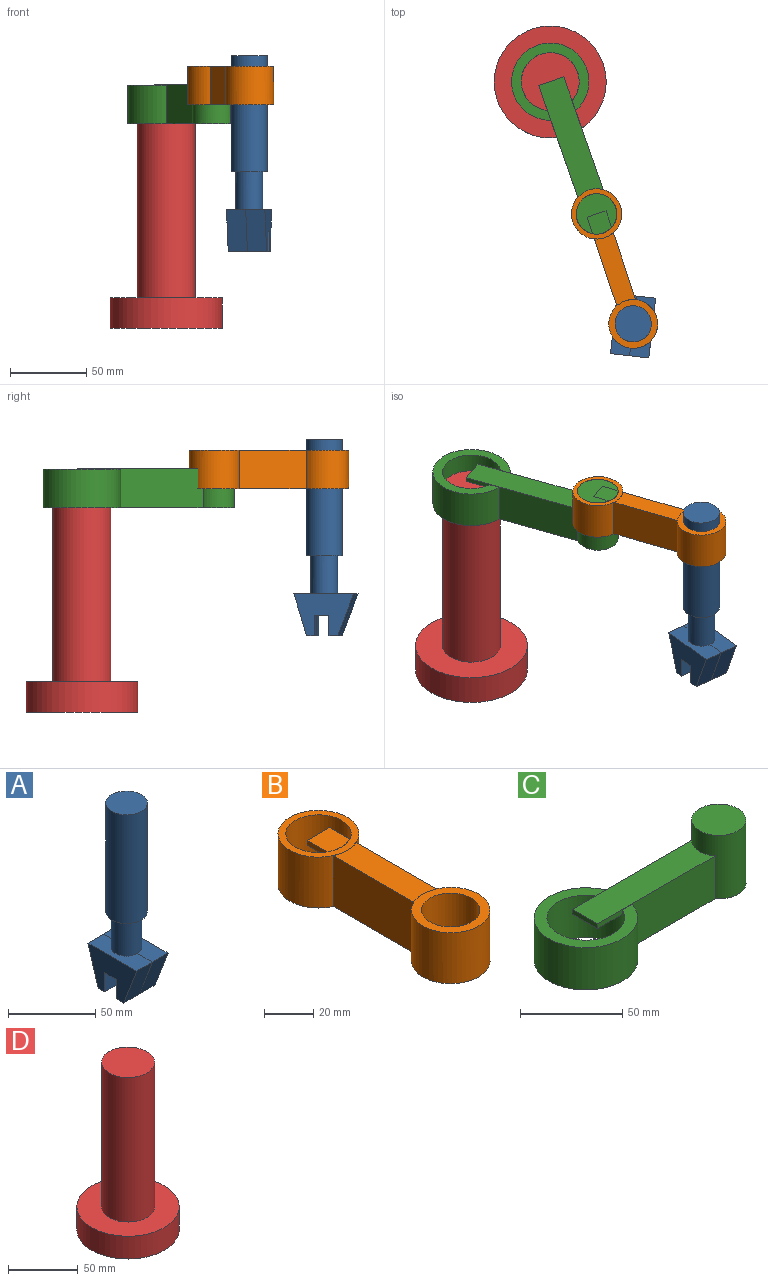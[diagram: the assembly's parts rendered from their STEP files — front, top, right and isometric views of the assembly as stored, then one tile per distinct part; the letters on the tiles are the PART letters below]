
ASSEMBLY  parts=4 mates=3
PART A: 23 faces, bbox 25.4x39.5x128.8 mm
  f0: cylinder r=8.8mm len=25.07mm, axis (0,0,1), area 1386.8mm2, adj f3,f4,f13,f14,f16
  f1: cylinder r=11.91mm len=76.2mm, axis (0,0,-1), area 5703.5mm2, adj f2,f3
  f2: plane 23.83x23.83mm, normal (0,0,1), area 445.8mm2, adj f1
  f3: plane 23.83x23.83mm, normal (0,0,-1), area 202.3mm2, adj f0,f1
  f4: plane 39.49x12.7mm, normal (0,0,1), area 379.8mm2, adj f0,f5,f11,f12,f13,f14
  f5: plane 27.55x12.71mm, normal (0,-0.93,-0.36), area 374.1mm2, adj f4,f6,f12,f17
  f6: plane 25.4x5.91mm, normal (0,0,-1), area 150.1mm2, adj f5,f7,f12,f17,f18,f22
  f7: plane 13.52x12.71mm, normal (0,1,0), area 171.6mm2, adj f6,f8,f12,f18
  f8: plane 12.71x9.62mm, normal (0,0,-1), area 122.1mm2, adj f7,f9,f12,f19
  f9: plane 13.51x12.7mm, normal (0,-1,0), area 171.6mm2, adj f8,f10,f12,f20
  f10: plane 12.71x5.2mm, normal (0,0,-1), area 66mm2, adj f9,f11,f12,f21
  f11: plane 27.54x12.7mm, normal (0,0.96,-0.29), area 365.4mm2, adj f4,f10,f12,f15
  f12: plane 39.49x27.54mm, normal (1,0,0), area 699.2mm2, adj f4,f5,f6,f7,f8,f9,f10,f11
  f13: plane 12.11x0.01mm, normal (1,0,0), area 0.1mm2, adj f0,f4,f16
  f14: plane 9.77x0mm, normal (1,0,0), area 0mm2, adj f0,f4,f16
  f15: plane 27.55x12.7mm, normal (0,0.96,-0.29), area 365.4mm2, adj f11,f16,f21,f22
  f16: plane 39.49x12.7mm, normal (0,0,1), area 379.8mm2, adj f0,f13,f14,f15,f17,f22
  f17: plane 27.56x12.71mm, normal (0,-0.93,-0.36), area 374.3mm2, adj f5,f6,f16,f22
  f18: plane 13.52x12.71mm, normal (0,1,0), area 171.6mm2, adj f6,f7,f19,f22
  f19: plane 12.71x9.62mm, normal (0,0,-1), area 122.1mm2, adj f8,f18,f20,f22
  f20: plane 13.51x12.7mm, normal (0,-1,0), area 171.6mm2, adj f9,f19,f21,f22
  f21: plane 12.71x5.2mm, normal (0,0,-1), area 66mm2, adj f10,f15,f20,f22
  f22: plane 39.49x27.56mm, normal (-1,0,0), area 699.2mm2, adj f6,f15,f16,f17,f18,f19,f20,f21
PART B: 15 faces, bbox 33x108.7x25.4 mm
  f0: plane 46.4x25.29mm, normal (-1,0,0), area 1173.3mm2, adj f2,f5,f10,f12
  f1: plane 46.4x25.29mm, normal (1,0,0), area 1173.3mm2, adj f2,f5,f10,f12
  f2: cylinder r=16.51mm len=33.02mm, axis (0,0,-1), area 2293.9mm2, adj f0,f1,f4,f5,f10
  f3: cylinder r=13.31mm len=26.62mm, axis (0,0,1), area 2091.2mm2, adj f4,f5,f7,f8,f9,f11
  f4: plane 33.02x33.02mm, normal (0,0,1), area 299.6mm2, adj f2,f3
  f5: plane 108.72x33.02mm, normal (0,0,-1), area 1245mm2, adj f0,f1,f2,f3,f12,f14
  f6: plane 13.11x2.43mm, normal (0,1,0), area 31.8mm2, adj f7,f8,f9,f11
  f7: plane 11.59x2.43mm, normal (-1,0,0), area 28.1mm2, adj f3,f6,f9,f11
  f8: plane 11.59x2.43mm, normal (1,0,0), area 28.1mm2, adj f3,f6,f9,f11
  f9: plane 13.31x13.11mm, normal (0,0,1), area 167.2mm2, adj f3,f6,f7,f8
  f10: plane 46.4x13.11mm, normal (0,0,1), area 584mm2, adj f0,f1,f2,f12
  f11: plane 13.31x13.11mm, normal (0,0,-1), area 167.2mm2, adj f3,f6,f7,f8
  f12: cylinder r=16.03mm len=32.06mm, axis (0,0,-1), area 2216.6mm2, adj f0,f1,f5,f10,f13
  f13: plane 32.06x32.06mm, normal (0,0,1), area 361.4mm2, adj f12,f14
  f14: cylinder r=11.91mm len=25.4mm, axis (0,0,1), area 1901.2mm2, adj f5,f13
PART C: 14 faces, bbox 130.9x50.8x38.1 mm
  f0: plane 81.53x25.7mm, normal (0,-1,0), area 1527.2mm2, adj f3,f5,f6,f7,f8,f10,f11,f12
  f1: plane 25.7x0.04mm, normal (0,1,0), area 1.1mm2, adj f4,f8,f9,f12
  f2: plane 82.75x25.7mm, normal (0,1,0), area 1569.5mm2, adj f3,f5,f6,f7,f8,f10,f11,f12
  f3: plane 82.75x17.44mm, normal (0,0,1), area 1393.6mm2, adj f0,f2,f10,f12
  f4: plane 25.7x0.04mm, normal (1,0,0), area 1.1mm2, adj f1,f8,f9,f12
  f5: cylinder r=25.4mm len=50.8mm, axis (0,0,-1), area 3601.2mm2, adj f0,f2,f6,f8
  f6: plane 50.8x49.5mm, normal (0,0,1), area 772.8mm2, adj f0,f2,f5,f7
  f7: cylinder r=19.05mm len=38.1mm, axis (0,0,1), area 2994.2mm2, adj f0,f2,f6,f8,f11
  f8: plane 130.86x50.8mm, normal (0,0,-1), area 2403mm2, adj f0,f1,f2,f4,f5,f7,f12
  f9: plane 0.04x0.04mm, normal (0,0,1), area 0mm2, adj f1,f4,f12
  f10: plane 17.44x2.84mm, normal (-1,0,0), area 49.6mm2, adj f0,f2,f3,f11
  f11: plane 19.05x17.44mm, normal (0,0,-1), area 320.1mm2, adj f0,f2,f7,f10
  f12: cylinder r=13.31mm len=38.1mm, axis (0,0,-1), area 2694.8mm2, adj f0,f1,f2,f3,f4,f8,f9,f13
  f13: plane 26.62x26.62mm, normal (0,0,1), area 556.7mm2, adj f12
PART D: 5 faces, bbox 73.5x73.5x147 mm
  f0: cylinder r=36.76mm len=73.52mm, axis (0,0,-1), area 4619.5mm2, adj f1,f2
  f1: plane 73.52x73.52mm, normal (0,0,1), area 3105.4mm2, adj f0,f3
  f2: plane 73.52x73.52mm, normal (0,0,-1), area 4245.5mm2, adj f0
  f3: cylinder r=19.05mm len=127mm, axis (0,0,-1), area 15201.2mm2, adj f1,f4
  f4: plane 38.1x38.1mm, normal (0,0,1), area 1140.1mm2, adj f3
PLACE A rot(axis=(0,0,-1),6.5deg) t=(-38.43,-165.07,101.3)mm
PLACE B rot(axis=(0,0,1),18.4deg) t=(-62.53,-92.8,145.28)mm
PLACE C rot(axis=(0,0,-1),70.7deg) t=(-92.99,-5.83,132.58)mm
PLACE D t=(-92.99,-5.83,-1.72)mm fixed
MATE cylindrical B.f12 <-> A.f1  axis (0,0,1) through (-38.43,-165.07,157.98)mm
MATE revolute C.f7 <-> D.f3  axis (0,0,1) through (-92.99,-5.83,145.28)mm
MATE revolute B.f3 <-> C.f12  axis (0,0,1) through (-62.53,-92.8,170.68)mm
